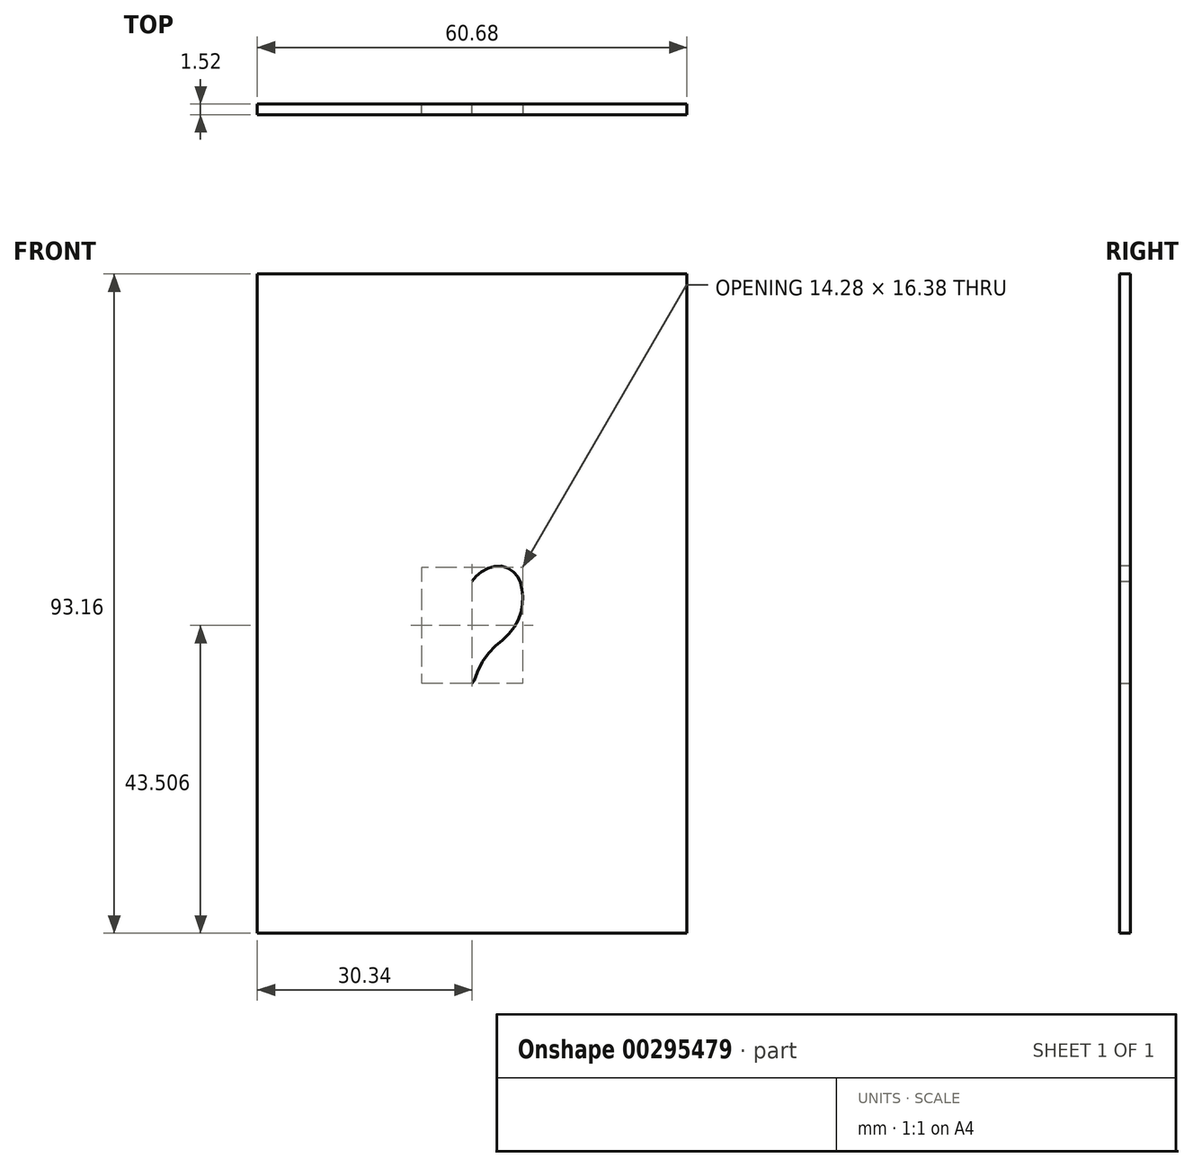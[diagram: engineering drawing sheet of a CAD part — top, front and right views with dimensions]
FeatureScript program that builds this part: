
annotation { "Feature Type Name" : "Feature", "Feature Type Description" : "" }
export const myFeature = defineFeature(function(context is Context, id is Id, definition is map)
    precondition{}
    {
        {
            var Q0;
            Q0=qCreatedBy(makeId("Front.planeOp"),FACE);
            var sketch = newSketch(context, id + "F0", { "sketchPlane" : qUnion([Q0])});
            skLineSegment(sketch, "E0.bottom", {"start": v(-30.34, 46.58) * mm, "end": v(30.34, 46.58) * mm});
            skLineSegment(sketch, "E0.top", {"start": v(-30.34, -46.58) * mm, "end": v(30.34, -46.58) * mm});
            skLineSegment(sketch, "E0.left", {"start": v(-30.34, 46.58) * mm, "end": v(-30.34, -46.58) * mm});
            skLineSegment(sketch, "E0.right", {"start": v(30.34, 46.58) * mm, "end": v(30.34, -46.58) * mm});
            skPoint(sketch, "E0.middle", {"position": v(0, 0) * mm});
            skFitSpline(sketch, "E1", {"points": [v(0, -11.27) * mm, v(1.49, -8.12) * mm, v(4.98, -4.5) * mm, v(6.85, -1.36) * mm, v(7.08, 1.9) * mm, v(6.26, 4) * mm, v(4.28, 5.28) * mm, v(1.84, 4.82) * mm, v(0, 3.19) * mm, v(0, 0) * mm, v(0, -11.27) * mm]});
            skFitSpline(sketch, "E2.MirrorC", {"points": [v(0, -11.27) * mm, v(-1.49, -8.12) * mm, v(-4.98, -4.5) * mm, v(-6.85, -1.36) * mm, v(-7.08, 1.9) * mm, v(-6.26, 4) * mm, v(-4.28, 5.28) * mm, v(-1.84, 4.82) * mm, v(0, 3.19) * mm, v(0, 0) * mm, v(0, -11.27) * mm]});
            skSolve(sketch);
        }
        {
            var Q0;
            Q0=makeQuery(id+"F0.imprint","IMPRINT",FACE,{"disambiguationData":[TD([[makeQuery(id+"F0.imprint","IMPRINT",EDGE,{"derivedFrom":sQuery(id+"F0.wireOp",EDGE,"E0.bottom")}),-1.0]])]});
            extrude(context, id + "F1", {"entities" : qUnion([Q0]), "endBound" : BoundingType.SYMMETRIC, "depth" : 1.52 * mm});
        }
    });
